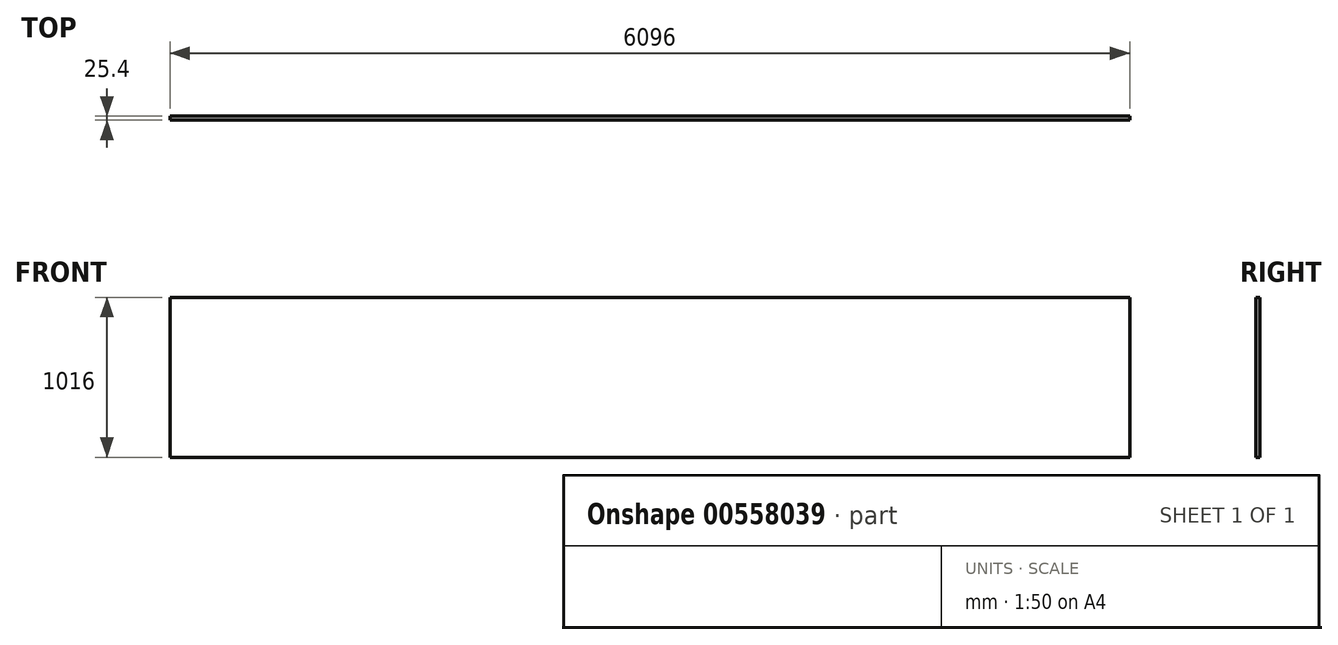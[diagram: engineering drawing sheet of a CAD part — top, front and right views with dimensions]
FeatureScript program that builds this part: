
annotation { "Feature Type Name" : "Feature", "Feature Type Description" : "" }
export const myFeature = defineFeature(function(context is Context, id is Id, definition is map)
    precondition{}
    {
        {
            var Q0;
            Q0=qCreatedBy(makeId("Front.planeOp"),FACE);
            var sketch = newSketch(context, id + "F0", { "sketchPlane" : qUnion([Q0])});
            skLineSegment(sketch, "E0.bottom", {"start": v(-3000.83, -272.64) * mm, "end": v(3095.17, -272.64) * mm});
            skLineSegment(sketch, "E0.top", {"start": v(-3000.83, 743.36) * mm, "end": v(3095.17, 743.36) * mm});
            skLineSegment(sketch, "E0.left", {"start": v(-3000.83, -272.64) * mm, "end": v(-3000.83, 743.36) * mm});
            skLineSegment(sketch, "E0.right", {"start": v(3095.17, -272.64) * mm, "end": v(3095.17, 743.36) * mm});
            skSolve(sketch);
        }
        {
            var Q0;
            Q0=makeQuery(id+"F0.imprint","IMPRINT",FACE,{"disambiguationData":[TD([[makeQuery(id+"F0.imprint","IMPRINT",EDGE,{"derivedFrom":sQuery(id+"F0.wireOp",EDGE,"E0.bottom")}),1.0]])]});
            extrude(context, id + "F1", {"entities" : qUnion([Q0]), "depth" : 25.4 * mm, "offsetDistance" : 25.4 * mm});
        }
    });
